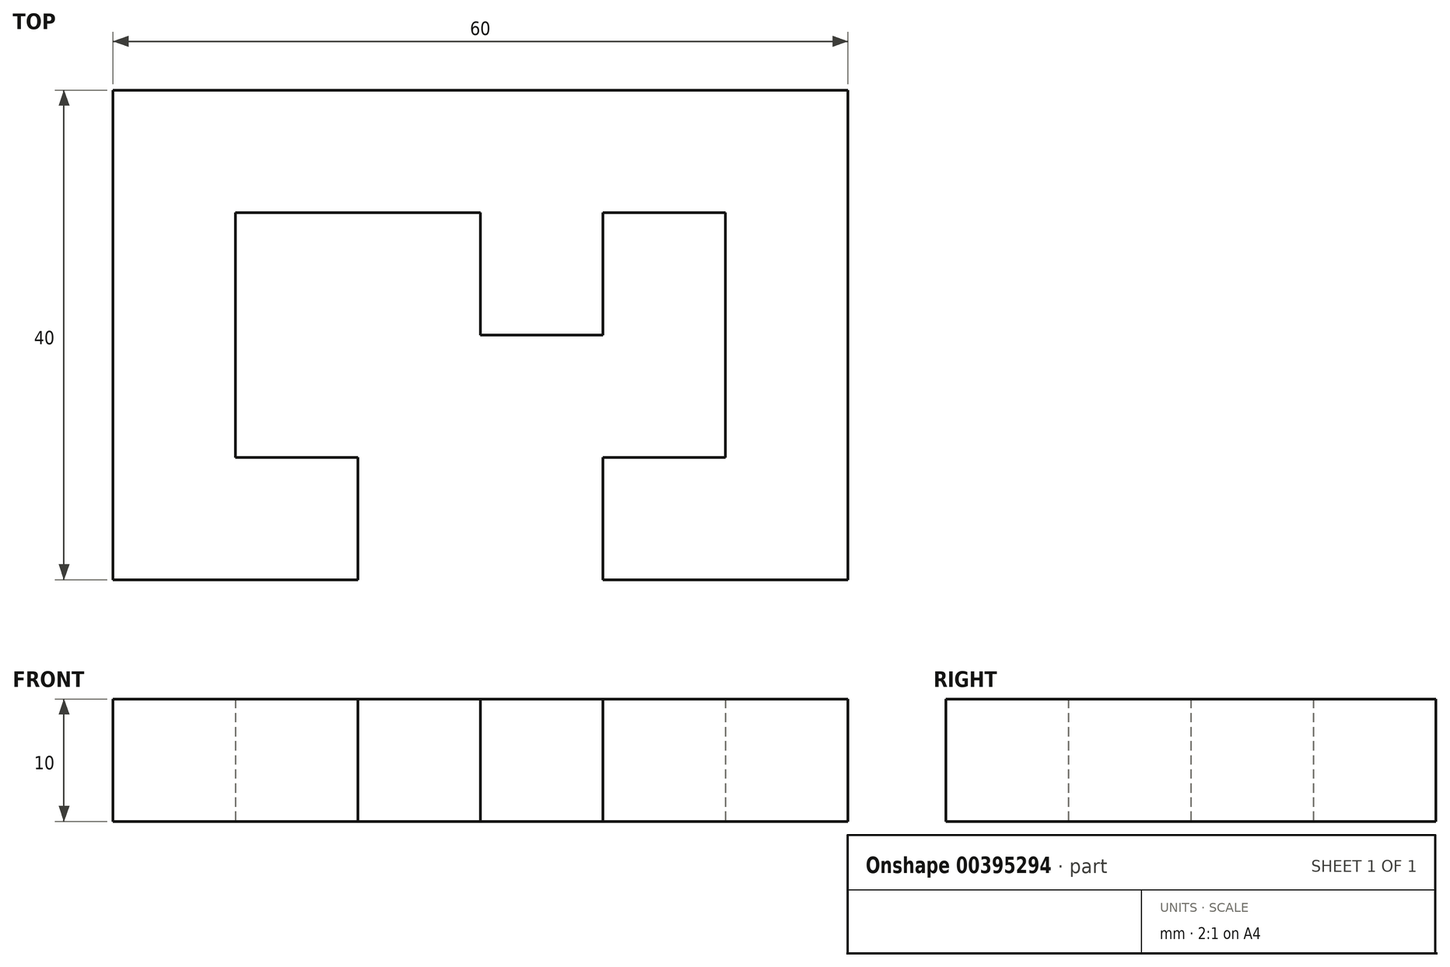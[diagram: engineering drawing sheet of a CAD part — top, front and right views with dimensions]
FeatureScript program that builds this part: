
annotation { "Feature Type Name" : "Feature", "Feature Type Description" : "" }
export const myFeature = defineFeature(function(context is Context, id is Id, definition is map)
    precondition{}
    {
        {
            var Q0;
            Q0=qCreatedBy(makeId("Top.planeOp"),FACE);
            var sketch = newSketch(context, id + "F0", { "sketchPlane" : qUnion([Q0])});
            skLineSegment(sketch, "E0.bottom", {"start": v(-30, 20) * mm, "end": v(30, 20) * mm});
            skLineSegment(sketch, "E0.top", {"start": v(-30, -20) * mm, "end": v(30, -20) * mm});
            skLineSegment(sketch, "E0.left", {"start": v(-30, 20) * mm, "end": v(-30, -20) * mm});
            skLineSegment(sketch, "E0.right", {"start": v(30, 20) * mm, "end": v(30, -20) * mm});
            skPoint(sketch, "E0.middle", {"position": v(0, 0) * mm});
            skLineSegment(sketch, "E1.bottom", {"start": v(-20, 10) * mm, "end": v(20, 10) * mm});
            skLineSegment(sketch, "E1.top", {"start": v(-20, -10) * mm, "end": v(20, -10) * mm});
            skLineSegment(sketch, "E1.left", {"start": v(-20, 10) * mm, "end": v(-20, -10) * mm});
            skLineSegment(sketch, "E1.right", {"start": v(20, 10) * mm, "end": v(20, -10) * mm});
            skLineSegment(sketch, "E2", {"start": v(-20, -10) * mm, "end": v(-10, -10) * mm, "construction": true});
            skLineSegment(sketch, "E3", {"start": v(-10, -10) * mm, "end": v(-10, -20) * mm});
            skLineSegment(sketch, "E4", {"start": v(-10, -10) * mm, "end": v(0, -10) * mm, "construction": true});
            skLineSegment(sketch, "E5", {"start": v(0, 0) * mm, "end": v(0, 10) * mm});
            skLineSegment(sketch, "E6", {"start": v(0, 10) * mm, "end": v(10, 10) * mm, "construction": true});
            skLineSegment(sketch, "E7", {"start": v(10, 10) * mm, "end": v(10, 0) * mm});
            skLineSegment(sketch, "E8", {"start": v(10, 0) * mm, "end": v(0, 0) * mm});
            skLineSegment(sketch, "E9", {"start": v(-10, -10) * mm, "end": v(10, -10) * mm, "construction": true});
            skLineSegment(sketch, "E10", {"start": v(10, -10) * mm, "end": v(10, -20) * mm});
            skSolve(sketch);
        }
        {
            var Q0;
            Q0=makeQuery(id+"F0.imprint","IMPRINT",FACE,{"disambiguationData":[TD([[makeQuery(id+"F0.imprint","IMPRINT",EDGE,{"derivedFrom":sQuery(id+"F0.wireOp",EDGE,"E0.bottom")}),-1.0]])]});
            var Q1;
            {var subQ0=sQuery(id+"F0.wireOp",EDGE,"E5");Q1=makeQuery(id+"F0.imprint","IMPRINT",FACE,{"disambiguationData":[TD([[makeQuery(id+"F0.imprint","IMPRINT",EDGE,{"derivedFrom":subQ0}),-1.0]])]});}
            extrude(context, id + "F1", {"entities" : qUnion([Q0, Q1]), "depth" : 10 * mm});
        }
    });
